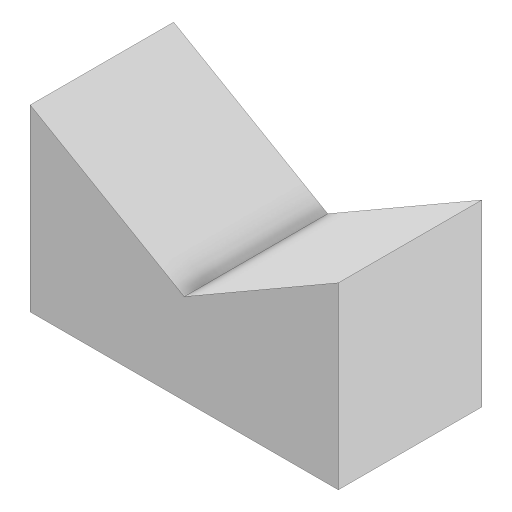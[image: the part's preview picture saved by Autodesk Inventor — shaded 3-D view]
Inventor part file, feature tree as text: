
AUTODESK INVENTOR PART (.ipt)
format: ipt  version: 2023.3 (Build 273359000, 359)  size: 113,664 bytes
history: native  units: mm
features: extrude x2, sketch x2
ambient origin geometry x8: Origin, YZ Plane, XZ Plane, XY Plane, X Axis, Y Axis, Z Axis, Center Point
bodies: Solid1 (feature_tree)
feature tree (4):
  extrude  "Extrusion1"  Depth=5.8mm
  extrude  "Extrusion2"  Depth=2.7mm TaperAngle=0.0deg
  sketch  "Sketch1"  dims[d0=5.5mm d1=5.8mm]
  sketch  "Sketch2"  dims[d2=6.376mm d3=2.7mm d4=0.0mm d5=1.0mm d6=1.0mm d7=2.0mm d8=1.5mm d9=0.0mm]
